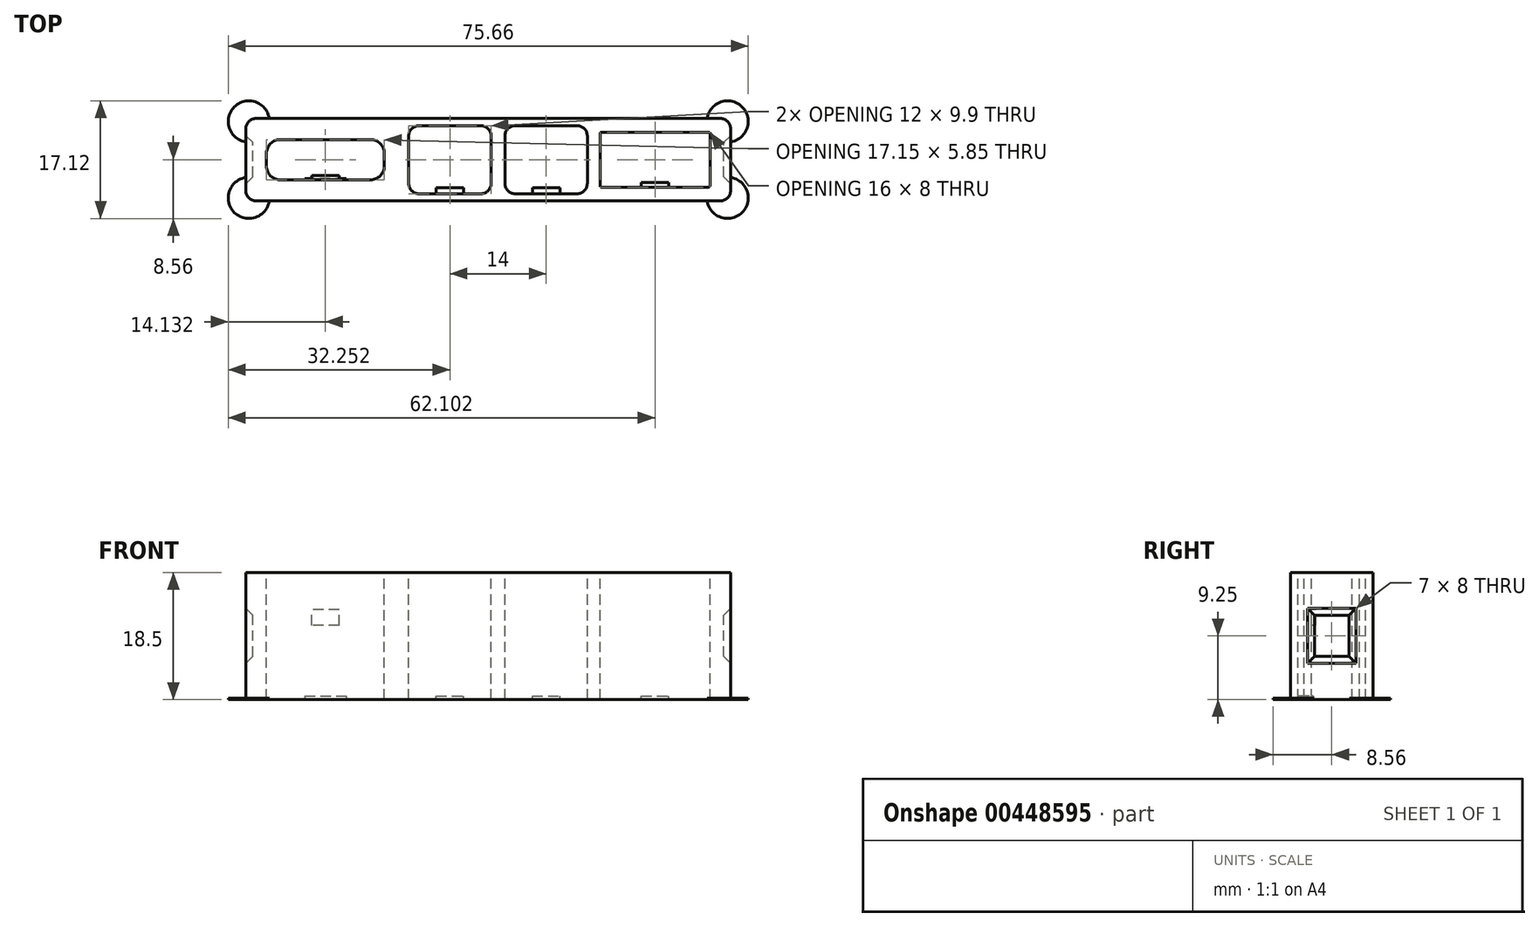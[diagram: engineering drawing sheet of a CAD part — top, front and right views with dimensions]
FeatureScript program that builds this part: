
annotation { "Feature Type Name" : "Feature", "Feature Type Description" : "" }
export const myFeature = defineFeature(function(context is Context, id is Id, definition is map)
    precondition{}
    {
        {
            assignVariable(context, id + "F0", {"name" : "TB1CableStopHeight", "anyValue" : .2});
        }
        {
            var Q0;
            Q0=qCreatedBy(makeId("Front.planeOp"),FACE);
            var sketch = newSketch(context, id + "F1", { "sketchPlane" : qUnion([Q0])});
            skLineSegment(sketch, "E0.bottom", {"start": v(33.77, -6) * mm, "end": v(-33.77, -6) * mm});
            skLineSegment(sketch, "E0.top", {"start": v(33.77, 6) * mm, "end": v(-33.77, 6) * mm});
            skLineSegment(sketch, "E0.left", {"start": v(35.27, -4.5) * mm, "end": v(35.27, 4.5) * mm});
            skLineSegment(sketch, "E0.right", {"start": v(-35.27, -4.5) * mm, "end": v(-35.27, 4.5) * mm});
            skPoint(sketch, "E0.middle", {"position": v(0, 0) * mm});
            skLineSegment(sketch, "E1", {"start": v(-35.27, 0) * mm, "end": v(35.27, 0) * mm, "construction": true});
            skLineSegment(sketch, "E2.bottom", {"start": v(-17.12, -2.92) * mm, "end": v(-30.27, -2.92) * mm});
            skLineSegment(sketch, "E2.top", {"start": v(-17.12, 2.93) * mm, "end": v(-30.27, 2.93) * mm});
            skLineSegment(sketch, "E2.left", {"start": v(-15.12, -0.92) * mm, "end": v(-15.12, 0.93) * mm});
            skLineSegment(sketch, "E2.right", {"start": v(-32.27, -0.92) * mm, "end": v(-32.27, 0.93) * mm});
            skPoint(sketch, "E2.middle", {"position": v(-23.7, 0) * mm});
            skLineSegment(sketch, "E3.bottom", {"start": v(-1.08, 4.95) * mm, "end": v(-10.08, 4.95) * mm});
            skLineSegment(sketch, "E3.top", {"start": v(-1.08, -4.95) * mm, "end": v(-10.08, -4.95) * mm});
            skLineSegment(sketch, "E3.left", {"start": v(0.42, 3.45) * mm, "end": v(0.42, -3.45) * mm});
            skLineSegment(sketch, "E3.right", {"start": v(-11.58, 3.45) * mm, "end": v(-11.58, -3.45) * mm});
            skPoint(sketch, "E3.middle", {"position": v(-5.58, 0) * mm});
            skLineSegment(sketch, "E4.bottom", {"start": v(12.92, 4.95) * mm, "end": v(3.92, 4.95) * mm});
            skLineSegment(sketch, "E4.top", {"start": v(12.92, -4.95) * mm, "end": v(3.92, -4.95) * mm});
            skLineSegment(sketch, "E4.left", {"start": v(14.42, 3.45) * mm, "end": v(14.42, -3.45) * mm});
            skLineSegment(sketch, "E4.right", {"start": v(2.42, 3.45) * mm, "end": v(2.42, -3.45) * mm});
            skPoint(sketch, "E4.middle", {"position": v(8.42, 0) * mm});
            skLineSegment(sketch, "E5.bottom", {"start": v(32.07, -4) * mm, "end": v(16.47, -4) * mm});
            skLineSegment(sketch, "E5.top", {"start": v(32.07, 4) * mm, "end": v(16.47, 4) * mm});
            skLineSegment(sketch, "E5.left", {"start": v(32.27, -3.8) * mm, "end": v(32.27, 3.8) * mm});
            skLineSegment(sketch, "E5.right", {"start": v(16.27, -3.8) * mm, "end": v(16.27, 3.8) * mm});
            skPoint(sketch, "E5.middle", {"position": v(24.27, 0) * mm});
            skPoint(sketch, "E6.visualSharp", {"position": v(-32.27, 2.93) * mm});
            skArc(sketch, "E6.filletArc", {"start": v(-30.27, 2.93) * mm, "mid": v(-31.69, 2.34) * mm, "end": v(-32.27, 0.93) * mm});
            skPoint(sketch, "E7.visualSharp", {"position": v(-15.12, 2.93) * mm});
            skArc(sketch, "E7.filletArc", {"start": v(-15.12, 0.93) * mm, "mid": v(-15.7, 2.34) * mm, "end": v(-17.12, 2.93) * mm});
            skPoint(sketch, "E8.visualSharp", {"position": v(-15.12, -2.92) * mm});
            skArc(sketch, "E8.filletArc", {"start": v(-17.12, -2.92) * mm, "mid": v(-15.7, -2.34) * mm, "end": v(-15.12, -0.92) * mm});
            skPoint(sketch, "E9.visualSharp", {"position": v(-32.27, -2.93) * mm});
            skArc(sketch, "E9.filletArc", {"start": v(-32.27, -0.92) * mm, "mid": v(-31.69, -2.34) * mm, "end": v(-30.27, -2.92) * mm});
            skPoint(sketch, "E10.visualSharp", {"position": v(-11.58, 4.95) * mm});
            skArc(sketch, "E10.filletArc", {"start": v(-10.08, 4.95) * mm, "mid": v(-11.14, 4.51) * mm, "end": v(-11.58, 3.45) * mm});
            skPoint(sketch, "E11.visualSharp", {"position": v(0.42, 4.95) * mm});
            skArc(sketch, "E11.filletArc", {"start": v(0.42, 3.45) * mm, "mid": v(-0.02, 4.51) * mm, "end": v(-1.08, 4.95) * mm});
            skPoint(sketch, "E12.visualSharp", {"position": v(-11.58, -4.95) * mm});
            skArc(sketch, "E12.filletArc", {"start": v(-11.58, -3.45) * mm, "mid": v(-11.14, -4.51) * mm, "end": v(-10.08, -4.95) * mm});
            skPoint(sketch, "E13.visualSharp", {"position": v(0.42, -4.95) * mm});
            skArc(sketch, "E13.filletArc", {"start": v(-1.08, -4.95) * mm, "mid": v(-0.02, -4.51) * mm, "end": v(0.42, -3.45) * mm});
            skPoint(sketch, "E14.visualSharp", {"position": v(2.42, 4.95) * mm});
            skArc(sketch, "E14.filletArc", {"start": v(3.92, 4.95) * mm, "mid": v(2.86, 4.51) * mm, "end": v(2.42, 3.45) * mm});
            skPoint(sketch, "E15.visualSharp", {"position": v(14.42, 4.95) * mm});
            skArc(sketch, "E15.filletArc", {"start": v(14.42, 3.45) * mm, "mid": v(13.98, 4.51) * mm, "end": v(12.92, 4.95) * mm});
            skPoint(sketch, "E16.visualSharp", {"position": v(14.42, -4.95) * mm});
            skArc(sketch, "E16.filletArc", {"start": v(12.92, -4.95) * mm, "mid": v(13.98, -4.51) * mm, "end": v(14.42, -3.45) * mm});
            skPoint(sketch, "E17.visualSharp", {"position": v(2.42, -4.95) * mm});
            skArc(sketch, "E17.filletArc", {"start": v(2.42, -3.45) * mm, "mid": v(2.86, -4.51) * mm, "end": v(3.92, -4.95) * mm});
            skPoint(sketch, "E18.visualSharp", {"position": v(16.27, 4) * mm});
            skArc(sketch, "E18.filletArc", {"start": v(16.47, 4) * mm, "mid": v(16.33, 3.94) * mm, "end": v(16.27, 3.8) * mm});
            skPoint(sketch, "E19.visualSharp", {"position": v(32.27, 4) * mm});
            skArc(sketch, "E19.filletArc", {"start": v(32.27, 3.8) * mm, "mid": v(32.21, 3.94) * mm, "end": v(32.07, 4) * mm});
            skPoint(sketch, "E20.visualSharp", {"position": v(32.27, -4) * mm});
            skArc(sketch, "E20.filletArc", {"start": v(32.07, -4) * mm, "mid": v(32.21, -3.94) * mm, "end": v(32.27, -3.8) * mm});
            skPoint(sketch, "E21.visualSharp", {"position": v(16.27, -4) * mm});
            skArc(sketch, "E21.filletArc", {"start": v(16.27, -3.8) * mm, "mid": v(16.33, -3.94) * mm, "end": v(16.47, -4) * mm});
            skPoint(sketch, "E22.visualSharp", {"position": v(-35.27, 6) * mm});
            skArc(sketch, "E22.filletArc", {"start": v(-33.77, 6) * mm, "mid": v(-34.83, 5.56) * mm, "end": v(-35.27, 4.5) * mm});
            skPoint(sketch, "E23.visualSharp", {"position": v(35.27, 6) * mm});
            skArc(sketch, "E23.filletArc", {"start": v(35.27, 4.5) * mm, "mid": v(34.83, 5.56) * mm, "end": v(33.77, 6) * mm});
            skPoint(sketch, "E24.visualSharp", {"position": v(35.27, -6) * mm});
            skArc(sketch, "E24.filletArc", {"start": v(33.77, -6) * mm, "mid": v(34.83, -5.56) * mm, "end": v(35.27, -4.5) * mm});
            skPoint(sketch, "E25.visualSharp", {"position": v(-35.27, -6) * mm});
            skArc(sketch, "E25.filletArc", {"start": v(-35.27, -4.5) * mm, "mid": v(-34.83, -5.56) * mm, "end": v(-33.77, -6) * mm});
            skSolve(sketch);
        }
        {
            var Q0;
            Q0=makeQuery(id+"F1.imprint","IMPRINT",FACE,{"disambiguationData":[TD([[makeQuery(id+"F1.imprint","IMPRINT",EDGE,{"derivedFrom":sQuery(id+"F1.wireOp",EDGE,"E0.bottom")}),-1.0]])]});
            extrude(context, id + "F2", {"entities" : qUnion([Q0]), "oppositeDirection" : true, "depth" : 18.5 * mm});
        }
        {
            var Q0;
            Q0=makeQuery(id+"F2.opExtrude","SWEPT_FACE",FACE,{"disambiguationData":[OSD([sQuery(id+"F1.wireOp",EDGE,"E0.top")])]});
            var sketch = newSketch(context, id + "F3", { "sketchPlane" : qUnion([Q0])});
            skPoint(sketch, "E26.0", {"position": v(-23.7, 0) * mm});
            skCircle(sketch, "E27", {"center": v(-23.7, 13.2) * mm, "radius": 1.55 * mm});
            skPoint(sketch, "E28.0", {"position": v(33.77, 9.25) * mm});
            skLineSegment(sketch, "E29.bottom", {"start": v(3.5, 13.25) * mm, "end": v(-3.5, 13.25) * mm});
            skLineSegment(sketch, "E29.top", {"start": v(3.5, 5.25) * mm, "end": v(-3.5, 5.25) * mm});
            skLineSegment(sketch, "E29.left", {"start": v(3.5, 13.25) * mm, "end": v(3.5, 5.25) * mm});
            skLineSegment(sketch, "E29.right", {"start": v(-3.5, 13.25) * mm, "end": v(-3.5, 5.25) * mm});
            skPoint(sketch, "E29.middle", {"position": v(0, 9.25) * mm});
            skSolve(sketch);
        }
        {
            var Q0;
            Q0=makeQuery(id+"F2.opExtrude","SWEPT_FACE",FACE,{"disambiguationData":[OSD([sQuery(id+"F1.wireOp",EDGE,"E2.bottom")])]});
            var sketch = newSketch(context, id + "F4", { "sketchPlane" : qUnion([Q0])});
            skPoint(sketch, "E30.0", {"position": v(-23.7, 0) * mm});
            skLineSegment(sketch, "E31.bottom", {"start": v(-26.7, 18) * mm, "end": v(-20.7, 18) * mm});
            skLineSegment(sketch, "E31.top", {"start": v(-26.7, 18.5) * mm, "end": v(-20.7, 18.5) * mm});
            skLineSegment(sketch, "E31.left", {"start": v(-26.7, 18) * mm, "end": v(-26.7, 18.5) * mm});
            skLineSegment(sketch, "E31.right", {"start": v(-20.7, 18) * mm, "end": v(-20.7, 18.5) * mm});
            skPoint(sketch, "E31.middle", {"position": v(-23.7, 18.25) * mm});
            skLineSegment(sketch, "E32.0", {"start": v(-17.12, 18.5) * mm, "end": v(-30.27, 18.5) * mm});
            skLineSegment(sketch, "E33.bottom", {"start": v(-21.7, 7.7) * mm, "end": v(-25.7, 7.7) * mm});
            skLineSegment(sketch, "E33.top", {"start": v(-21.7, 5.45) * mm, "end": v(-25.7, 5.45) * mm});
            skLineSegment(sketch, "E33.left", {"start": v(-21.7, 7.7) * mm, "end": v(-21.7, 5.45) * mm});
            skLineSegment(sketch, "E33.right", {"start": v(-25.7, 7.7) * mm, "end": v(-25.7, 5.45) * mm});
            skPoint(sketch, "E33.middle", {"position": v(-23.7, 6.57) * mm});
            skSolve(sketch);
        }
        {
            var Q0;
            Q0=makeQuery(id+"F4.imprint","IMPRINT",FACE,{"disambiguationData":[TD([[makeQuery(id+"F4.imprint","IMPRINT",EDGE,{"derivedFrom":sQuery(id+"F4.wireOp",EDGE,"E31.bottom")}),1.0]])]});
            extrude(context, id + "F5", {"entities" : qUnion([Q0]), "operationType" : NewBodyOperationType.ADD, "depth" : .2 * mm});
        }
        {
            var Q0;
            Q0=makeQuery(id+"F4.imprint","IMPRINT",FACE,{"disambiguationData":[TD([[makeQuery(id+"F4.imprint","IMPRINT",EDGE,{"derivedFrom":sQuery(id+"F4.wireOp",EDGE,"E33.bottom")}),1.0]])]});
            extrude(context, id + "F6", {"entities" : qUnion([Q0]), "operationType" : NewBodyOperationType.ADD, "depth" : .6 * mm});
        }
        {
            var Q0;
            Q0=makeQuery(id+"F2.opExtrude","SWEPT_FACE",FACE,{"disambiguationData":[OSD([sQuery(id+"F1.wireOp",EDGE,"E3.top")])]});
            var sketch = newSketch(context, id + "F7", { "sketchPlane" : qUnion([Q0])});
            skPoint(sketch, "E34.0", {"position": v(-5.58, 0) * mm});
            skLineSegment(sketch, "E35.bottom", {"start": v(-7.58, 18.5) * mm, "end": v(-3.58, 18.5) * mm});
            skLineSegment(sketch, "E35.top", {"start": v(-7.58, 18) * mm, "end": v(-3.58, 18) * mm});
            skLineSegment(sketch, "E35.left", {"start": v(-7.58, 18.5) * mm, "end": v(-7.58, 18) * mm});
            skLineSegment(sketch, "E35.right", {"start": v(-3.58, 18.5) * mm, "end": v(-3.58, 18) * mm});
            skPoint(sketch, "E35.middle", {"position": v(-5.58, 18.25) * mm});
            skLineSegment(sketch, "E36.bottom", {"start": v(-3.58, -1.5) * mm, "end": v(-7.58, -1.5) * mm});
            skLineSegment(sketch, "E36.top", {"start": v(-3.58, 0) * mm, "end": v(-7.58, 0) * mm});
            skLineSegment(sketch, "E36.left", {"start": v(-3.58, -1.5) * mm, "end": v(-3.58, 0) * mm});
            skLineSegment(sketch, "E36.right", {"start": v(-7.58, -1.5) * mm, "end": v(-7.58, 0) * mm});
            skPoint(sketch, "E36.middle", {"position": v(-5.58, -0.75) * mm});
            skLineSegment(sketch, "E37.0", {"start": v(-1.08, 18.5) * mm, "end": v(-10.08, 18.5) * mm});
            skSolve(sketch);
        }
        {
            var Q0;
            Q0=makeQuery(id+"F7.imprint","IMPRINT",FACE,{"disambiguationData":[TD([[makeQuery(id+"F7.imprint","IMPRINT",EDGE,{"derivedFrom":sQuery(id+"F7.wireOp",EDGE,"E35.top")}),1.0]])]});
            extrude(context, id + "F8", {"entities" : qUnion([Q0]), "operationType" : NewBodyOperationType.ADD, "depth" : .9 * mm});
        }
        {
            var Q0;
            {var subQ0=sQuery(id+"F7.wireOp",EDGE,"E36.top");Q0=makeQuery(id+"F7.imprint","IMPRINT",FACE,{"disambiguationData":[TD([[makeQuery(id+"F7.imprint","IMPRINT",EDGE,{"derivedFrom":subQ0}),1.0]])]});}
            extrude(context, id + "F9", {"entities" : qUnion([Q0]), "operationType" : NewBodyOperationType.ADD, "depth" : (getVariable(context, 'TB1CableStopHeight')) * mm});
        }
        {
            var Q0;
            Q0=makeQuery(id+"F2.opExtrude","SWEPT_FACE",FACE,{"disambiguationData":[OSD([sQuery(id+"F1.wireOp",EDGE,"E4.top")])]});
            var sketch = newSketch(context, id + "F10", { "sketchPlane" : qUnion([Q0])});
            skPoint(sketch, "E38.0", {"position": v(8.42, 0) * mm});
            skLineSegment(sketch, "E39.bottom", {"start": v(6.42, 18.5) * mm, "end": v(10.42, 18.5) * mm});
            skLineSegment(sketch, "E39.top", {"start": v(6.42, 18) * mm, "end": v(10.42, 18) * mm});
            skLineSegment(sketch, "E39.left", {"start": v(6.42, 18.5) * mm, "end": v(6.42, 18) * mm});
            skLineSegment(sketch, "E39.right", {"start": v(10.42, 18.5) * mm, "end": v(10.42, 18) * mm});
            skPoint(sketch, "E39.middle", {"position": v(8.42, 18.25) * mm});
            skLineSegment(sketch, "E40.bottom", {"start": v(10.42, 0) * mm, "end": v(6.42, 0) * mm});
            skLineSegment(sketch, "E40.top", {"start": v(10.42, -1.5) * mm, "end": v(6.42, -1.5) * mm});
            skLineSegment(sketch, "E40.left", {"start": v(10.42, 0) * mm, "end": v(10.42, -1.5) * mm});
            skLineSegment(sketch, "E40.right", {"start": v(6.42, 0) * mm, "end": v(6.42, -1.5) * mm});
            skPoint(sketch, "E40.middle", {"position": v(8.42, -0.75) * mm});
            skLineSegment(sketch, "E41.0", {"start": v(12.92, 18.5) * mm, "end": v(3.92, 18.5) * mm});
            skSolve(sketch);
        }
        {
            var Q0;
            Q0=makeQuery(id+"F10.imprint","IMPRINT",FACE,{"disambiguationData":[TD([[makeQuery(id+"F10.imprint","IMPRINT",EDGE,{"derivedFrom":sQuery(id+"F10.wireOp",EDGE,"E39.top")}),1.0]])]});
            extrude(context, id + "F11", {"entities" : qUnion([Q0]), "operationType" : NewBodyOperationType.ADD, "depth" : .9 * mm});
        }
        {
            var Q0;
            Q0=makeQuery(id+"F10.imprint","IMPRINT",FACE,{"disambiguationData":[TD([[makeQuery(id+"F10.imprint","IMPRINT",EDGE,{"derivedFrom":sQuery(id+"F10.wireOp",EDGE,"E40.bottom")}),1.0]])]});
            extrude(context, id + "F12", {"entities" : qUnion([Q0]), "operationType" : NewBodyOperationType.ADD, "depth" : (getVariable(context, 'TB1CableStopHeight')) * mm});
        }
        {
            var Q0;
            Q0=makeQuery(id+"F2.opExtrude","SWEPT_FACE",FACE,{"disambiguationData":[OSD([sQuery(id+"F1.wireOp",EDGE,"E5.bottom")])]});
            var sketch = newSketch(context, id + "F13", { "sketchPlane" : qUnion([Q0])});
            skPoint(sketch, "E42.0", {"position": v(24.27, 0) * mm});
            skLineSegment(sketch, "E43.bottom", {"start": v(22.27, 18.5) * mm, "end": v(26.27, 18.5) * mm});
            skLineSegment(sketch, "E43.top", {"start": v(22.27, 18) * mm, "end": v(26.27, 18) * mm});
            skLineSegment(sketch, "E43.left", {"start": v(22.27, 18.5) * mm, "end": v(22.27, 18) * mm});
            skLineSegment(sketch, "E43.right", {"start": v(26.27, 18.5) * mm, "end": v(26.27, 18) * mm});
            skPoint(sketch, "E43.middle", {"position": v(24.27, 18.25) * mm});
            skSolve(sketch);
        }
        {
            var Q0;
            Q0=makeQuery(id+"F13.imprint","IMPRINT",FACE,{"disambiguationData":[TD([[makeQuery(id+"F13.imprint","IMPRINT",EDGE,{"derivedFrom":sQuery(id+"F13.wireOp",EDGE,"E43.bottom")}),1.0]])]});
            extrude(context, id + "F14", {"entities" : qUnion([Q0]), "operationType" : NewBodyOperationType.ADD, "depth" : .7 * mm});
        }
        {
            var Q0;
            Q0=makeQuery(id+"F2.opExtrude","SWEPT_FACE",FACE,{"disambiguationData":[OSD([sQuery(id+"F1.wireOp",EDGE,"E0.left")])]});
            var sketch = newSketch(context, id + "F15", { "sketchPlane" : qUnion([Q0])});
            skPoint(sketch, "E44.0", {"position": v(9.25, 6) * mm});
            skPoint(sketch, "E45.0", {"position": v(18.5, 0) * mm});
            skLineSegment(sketch, "E46.bottom", {"start": v(13.25, 3.5) * mm, "end": v(5.25, 3.5) * mm});
            skLineSegment(sketch, "E46.top", {"start": v(13.25, -3.5) * mm, "end": v(5.25, -3.5) * mm});
            skLineSegment(sketch, "E46.left", {"start": v(13.25, 3.5) * mm, "end": v(13.25, -3.5) * mm});
            skLineSegment(sketch, "E46.right", {"start": v(5.25, 3.5) * mm, "end": v(5.25, -3.5) * mm});
            skPoint(sketch, "E46.middle", {"position": v(9.25, 0) * mm});
            skSolve(sketch);
        }
        {
            var Q0;
            Q0=qSketchRegion(id+"F15",true);
            extrude(context, id + "F16", {"entities" : qUnion([Q0]), "operationType" : NewBodyOperationType.REMOVE, "oppositeDirection" : true, "depth" : 1 * mm, "hasDraft" : true, "draftAngle" : 45 * degree, "draftPullDirection" : true});
        }
        {
            var Q0;
            Q0=makeQuery(id+"F2.opExtrude","SWEPT_FACE",FACE,{"disambiguationData":[OSD([sQuery(id+"F1.wireOp",EDGE,"E0.right")])]});
            var sketch = newSketch(context, id + "F17", { "sketchPlane" : qUnion([Q0])});
            skPoint(sketch, "E47.0", {"position": v(-9.25, 6) * mm});
            skPoint(sketch, "E48.0", {"position": v(0, 0) * mm});
            skLineSegment(sketch, "E49.bottom", {"start": v(-5.25, -3.5) * mm, "end": v(-13.25, -3.5) * mm});
            skLineSegment(sketch, "E49.top", {"start": v(-5.25, 3.5) * mm, "end": v(-13.25, 3.5) * mm});
            skLineSegment(sketch, "E49.left", {"start": v(-5.25, -3.5) * mm, "end": v(-5.25, 3.5) * mm});
            skLineSegment(sketch, "E49.right", {"start": v(-13.25, -3.5) * mm, "end": v(-13.25, 3.5) * mm});
            skPoint(sketch, "E49.middle", {"position": v(-9.25, 0) * mm});
            skSolve(sketch);
        }
        {
            var Q0;
            Q0=qSketchRegion(id+"F17",true);
            extrude(context, id + "F18", {"entities" : qUnion([Q0]), "operationType" : NewBodyOperationType.REMOVE, "oppositeDirection" : true, "depth" : 1 * mm, "hasDraft" : true, "draftAngle" : 45 * degree, "draftPullDirection" : true});
        }
        {
            var Q0;
            Q0=makeQuery(id+"F2.opExtrude","SWEPT_FACE",FACE,{"disambiguationData":[OSD([sQuery(id+"F1.wireOp",EDGE,"E0.bottom")])]});
            var sketch = newSketch(context, id + "F19", { "sketchPlane" : qUnion([Q0])});
            skPoint(sketch, "E50.0", {"position": v(-38.78, -17.75) * mm});
            skPoint(sketch, "E51.0", {"position": v(0, 0) * mm});
            skPoint(sketch, "E52.0", {"position": v(33.77, -9.25) * mm});
            skLineSegment(sketch, "E53.bottom", {"start": v(4, -5.75) * mm, "end": v(-4, -5.75) * mm});
            skLineSegment(sketch, "E53.top", {"start": v(4, -12.75) * mm, "end": v(-4, -12.75) * mm});
            skLineSegment(sketch, "E53.left", {"start": v(4, -5.75) * mm, "end": v(4, -12.75) * mm});
            skLineSegment(sketch, "E53.right", {"start": v(-4, -5.75) * mm, "end": v(-4, -12.75) * mm});
            skPoint(sketch, "E53.middle", {"position": v(0, -9.25) * mm});
            skText(sketch, "E54", { "text": "JS", "fontName": "OpenSans-Regular.ttf"});
            const initialGuessF19  = {"E54": [0.0279, -0.01727, 1, 0, 0.00333]};
            skSetInitialGuess(sketch, initialGuessF19);
            skSolve(sketch);
        }
        {
            var Q0;
            Q0=makeQuery(id+"F14.boolean.opBoolean","MERGE",FACE,{"derivedFrom":[makeQuery(id+"F11.boolean.opBoolean","MERGE",FACE,{"derivedFrom":[makeQuery(id+"F8.boolean.opBoolean","MERGE",FACE,{"derivedFrom":[makeQuery(id+"F5.boolean.opBoolean","MERGE",FACE,{"derivedFrom":[makeQuery(id+"F2.opExtrude","CAP_FACE",FACE,{"disambiguationData":[OSD([sQuery(id+"F1.wireOp",EDGE,"E0.bottom"),sQuery(id+"F1.wireOp",EDGE,"E0.top"),sQuery(id+"F1.wireOp",EDGE,"E0.left"),sQuery(id+"F1.wireOp",EDGE,"E0.right"),sQuery(id+"F1.wireOp",EDGE,"E2.bottom"),sQuery(id+"F1.wireOp",EDGE,"E2.top"),sQuery(id+"F1.wireOp",EDGE,"E2.left"),sQuery(id+"F1.wireOp",EDGE,"E2.right"),sQuery(id+"F1.wireOp",EDGE,"E3.bottom"),sQuery(id+"F1.wireOp",EDGE,"E3.top"),sQuery(id+"F1.wireOp",EDGE,"E3.left"),sQuery(id+"F1.wireOp",EDGE,"E3.right"),sQuery(id+"F1.wireOp",EDGE,"E4.bottom"),sQuery(id+"F1.wireOp",EDGE,"E4.top"),sQuery(id+"F1.wireOp",EDGE,"E4.left"),sQuery(id+"F1.wireOp",EDGE,"E4.right"),sQuery(id+"F1.wireOp",EDGE,"E5.bottom"),sQuery(id+"F1.wireOp",EDGE,"E5.top"),sQuery(id+"F1.wireOp",EDGE,"E5.left"),sQuery(id+"F1.wireOp",EDGE,"E5.right"),sQuery(id+"F1.wireOp",EDGE,"E6.filletArc"),sQuery(id+"F1.wireOp",EDGE,"E7.filletArc"),sQuery(id+"F1.wireOp",EDGE,"E8.filletArc"),sQuery(id+"F1.wireOp",EDGE,"E9.filletArc"),sQuery(id+"F1.wireOp",EDGE,"E10.filletArc"),sQuery(id+"F1.wireOp",EDGE,"E11.filletArc"),sQuery(id+"F1.wireOp",EDGE,"E12.filletArc"),sQuery(id+"F1.wireOp",EDGE,"E13.filletArc"),sQuery(id+"F1.wireOp",EDGE,"E14.filletArc"),sQuery(id+"F1.wireOp",EDGE,"E15.filletArc"),sQuery(id+"F1.wireOp",EDGE,"E16.filletArc"),sQuery(id+"F1.wireOp",EDGE,"E17.filletArc"),sQuery(id+"F1.wireOp",EDGE,"E18.filletArc"),sQuery(id+"F1.wireOp",EDGE,"E19.filletArc"),sQuery(id+"F1.wireOp",EDGE,"E20.filletArc"),sQuery(id+"F1.wireOp",EDGE,"E21.filletArc"),sQuery(id+"F1.wireOp",EDGE,"E22.filletArc"),sQuery(id+"F1.wireOp",EDGE,"E23.filletArc"),sQuery(id+"F1.wireOp",EDGE,"E24.filletArc"),sQuery(id+"F1.wireOp",EDGE,"E25.filletArc")])],"isStart":false}),makeQuery(id+"F5.opExtrude","SWEPT_FACE",FACE,{"disambiguationData":[OSD([sQuery(id+"F4.wireOp",EDGE,"E32.0")])]})]}),makeQuery(id+"F8.opExtrude","SWEPT_FACE",FACE,{"disambiguationData":[OSD([sQuery(id+"F7.wireOp",EDGE,"E37.0")])]})]}),makeQuery(id+"F11.opExtrude","SWEPT_FACE",FACE,{"disambiguationData":[OSD([sQuery(id+"F10.wireOp",EDGE,"E41.0")])]})]}),makeQuery(id+"F14.opExtrude","SWEPT_FACE",FACE,{"disambiguationData":[OSD([sQuery(id+"F13.wireOp",EDGE,"E43.bottom")])]})]});
            var sketch = newSketch(context, id + "F20", { "sketchPlane" : qUnion([Q0])});
            skCircle(sketch, "E55", {"center": v(-34.83, 5.56) * mm, "radius": 3 * mm});
            skCircle(sketch, "E56", {"center": v(34.83, 5.56) * mm, "radius": 3 * mm});
            skCircle(sketch, "E57", {"center": v(34.83, -5.56) * mm, "radius": 3 * mm});
            skCircle(sketch, "E58", {"center": v(-34.83, -5.56) * mm, "radius": 3 * mm});
            skSolve(sketch);
        }
        {
            var Q0;
            {var subQ5=makeQuery(id+"F2.opExtrude","CAP_EDGE",EDGE,{"disambiguationData":[OSD([sQuery(id+"F1.wireOp",EDGE,"E23.filletArc")])],"isStart":false});Q0=makeQuery(id+"F20.imprint","IMPRINT",FACE,{"disambiguationData":[TD([[makeQuery(id+"F20.imprint","IMPRINT",EDGE,{"derivedFrom":subQ5}),1.0]])]});}
            var Q1;
            {var subQ5=makeQuery(id+"F2.opExtrude","CAP_EDGE",EDGE,{"disambiguationData":[OSD([sQuery(id+"F1.wireOp",EDGE,"E24.filletArc")])],"isStart":false});Q1=makeQuery(id+"F20.imprint","IMPRINT",FACE,{"disambiguationData":[TD([[makeQuery(id+"F20.imprint","IMPRINT",EDGE,{"derivedFrom":subQ5}),1.0]])]});}
            var Q2;
            {var subQ5=makeQuery(id+"F2.opExtrude","CAP_EDGE",EDGE,{"disambiguationData":[OSD([sQuery(id+"F1.wireOp",EDGE,"E22.filletArc")])],"isStart":false});Q2=makeQuery(id+"F20.imprint","IMPRINT",FACE,{"disambiguationData":[TD([[makeQuery(id+"F20.imprint","IMPRINT",EDGE,{"derivedFrom":subQ5}),1.0]])]});}
            var Q3;
            {var subQ5=makeQuery(id+"F2.opExtrude","CAP_EDGE",EDGE,{"disambiguationData":[OSD([sQuery(id+"F1.wireOp",EDGE,"E25.filletArc")])],"isStart":false});Q3=makeQuery(id+"F20.imprint","IMPRINT",FACE,{"disambiguationData":[TD([[makeQuery(id+"F20.imprint","IMPRINT",EDGE,{"derivedFrom":subQ5}),1.0]])]});}
            extrude(context, id + "F21", {"entities" : qUnion([Q0, Q1, Q2, Q3]), "operationType" : NewBodyOperationType.ADD, "oppositeDirection" : true, "depth" : .2 * mm});
        }
        {
            var Q0;
            Q0=makeQuery(id+"F2.opExtrude","SWEPT_BODY",BODY,{"disambiguationData":[OSD([sQuery(id+"F1.wireOp",EDGE,"E0.bottom"),sQuery(id+"F1.wireOp",EDGE,"E0.top"),sQuery(id+"F1.wireOp",EDGE,"E0.left"),sQuery(id+"F1.wireOp",EDGE,"E0.right"),sQuery(id+"F1.wireOp",EDGE,"E2.bottom"),sQuery(id+"F1.wireOp",EDGE,"E2.top"),sQuery(id+"F1.wireOp",EDGE,"E2.left"),sQuery(id+"F1.wireOp",EDGE,"E2.right"),sQuery(id+"F1.wireOp",EDGE,"E3.bottom"),sQuery(id+"F1.wireOp",EDGE,"E3.top"),sQuery(id+"F1.wireOp",EDGE,"E3.left"),sQuery(id+"F1.wireOp",EDGE,"E3.right"),sQuery(id+"F1.wireOp",EDGE,"E4.bottom"),sQuery(id+"F1.wireOp",EDGE,"E4.top"),sQuery(id+"F1.wireOp",EDGE,"E4.left"),sQuery(id+"F1.wireOp",EDGE,"E4.right"),sQuery(id+"F1.wireOp",EDGE,"E5.bottom"),sQuery(id+"F1.wireOp",EDGE,"E5.top"),sQuery(id+"F1.wireOp",EDGE,"E5.left"),sQuery(id+"F1.wireOp",EDGE,"E5.right"),sQuery(id+"F1.wireOp",EDGE,"E6.filletArc"),sQuery(id+"F1.wireOp",EDGE,"E7.filletArc"),sQuery(id+"F1.wireOp",EDGE,"E8.filletArc"),sQuery(id+"F1.wireOp",EDGE,"E9.filletArc"),sQuery(id+"F1.wireOp",EDGE,"E10.filletArc"),sQuery(id+"F1.wireOp",EDGE,"E11.filletArc"),sQuery(id+"F1.wireOp",EDGE,"E12.filletArc"),sQuery(id+"F1.wireOp",EDGE,"E13.filletArc"),sQuery(id+"F1.wireOp",EDGE,"E14.filletArc"),sQuery(id+"F1.wireOp",EDGE,"E15.filletArc"),sQuery(id+"F1.wireOp",EDGE,"E16.filletArc"),sQuery(id+"F1.wireOp",EDGE,"E17.filletArc"),sQuery(id+"F1.wireOp",EDGE,"E18.filletArc"),sQuery(id+"F1.wireOp",EDGE,"E19.filletArc"),sQuery(id+"F1.wireOp",EDGE,"E20.filletArc"),sQuery(id+"F1.wireOp",EDGE,"E21.filletArc"),sQuery(id+"F1.wireOp",EDGE,"E22.filletArc"),sQuery(id+"F1.wireOp",EDGE,"E23.filletArc"),sQuery(id+"F1.wireOp",EDGE,"E24.filletArc"),sQuery(id+"F1.wireOp",EDGE,"E25.filletArc")])]});
            var Q1;
            Q1=makeQuery(id+"F2.opExtrude","CAP_EDGE",EDGE,{"disambiguationData":[OSD([sQuery(id+"F1.wireOp",EDGE,"E0.top")])],"isStart":false});
            transform(context, id + "F22", {"entities" : qUnion([Q0]), "transformType" : TransformType.ROTATION, "transformAxis" : qUnion([Q1]), "angle" : 90 * degree, "makeCopy" : false});
        }
        {
            var Q0;
            Q0=makeQuery(id+"F12.opExtrude","SWEPT_BODY",BODY,{"disambiguationData":[OSD([sQuery(id+"F10.wireOp",EDGE,"E40.bottom"),sQuery(id+"F10.wireOp",EDGE,"E40.top"),sQuery(id+"F10.wireOp",EDGE,"E40.left"),sQuery(id+"F10.wireOp",EDGE,"E40.right")])]});
            deleteBodies(context, id + "F23", {"entities" : qUnion([Q0])});
        }
        {
            var Q0;
            Q0=makeQuery(id+"F9.opExtrude","SWEPT_BODY",BODY,{"disambiguationData":[OSD([sQuery(id+"F7.wireOp",EDGE,"E36.bottom"),sQuery(id+"F7.wireOp",EDGE,"E36.top"),sQuery(id+"F7.wireOp",EDGE,"E36.left"),sQuery(id+"F7.wireOp",EDGE,"E36.right")])]});
            deleteBodies(context, id + "F24", {"entities" : qUnion([Q0])});
        }
    });
